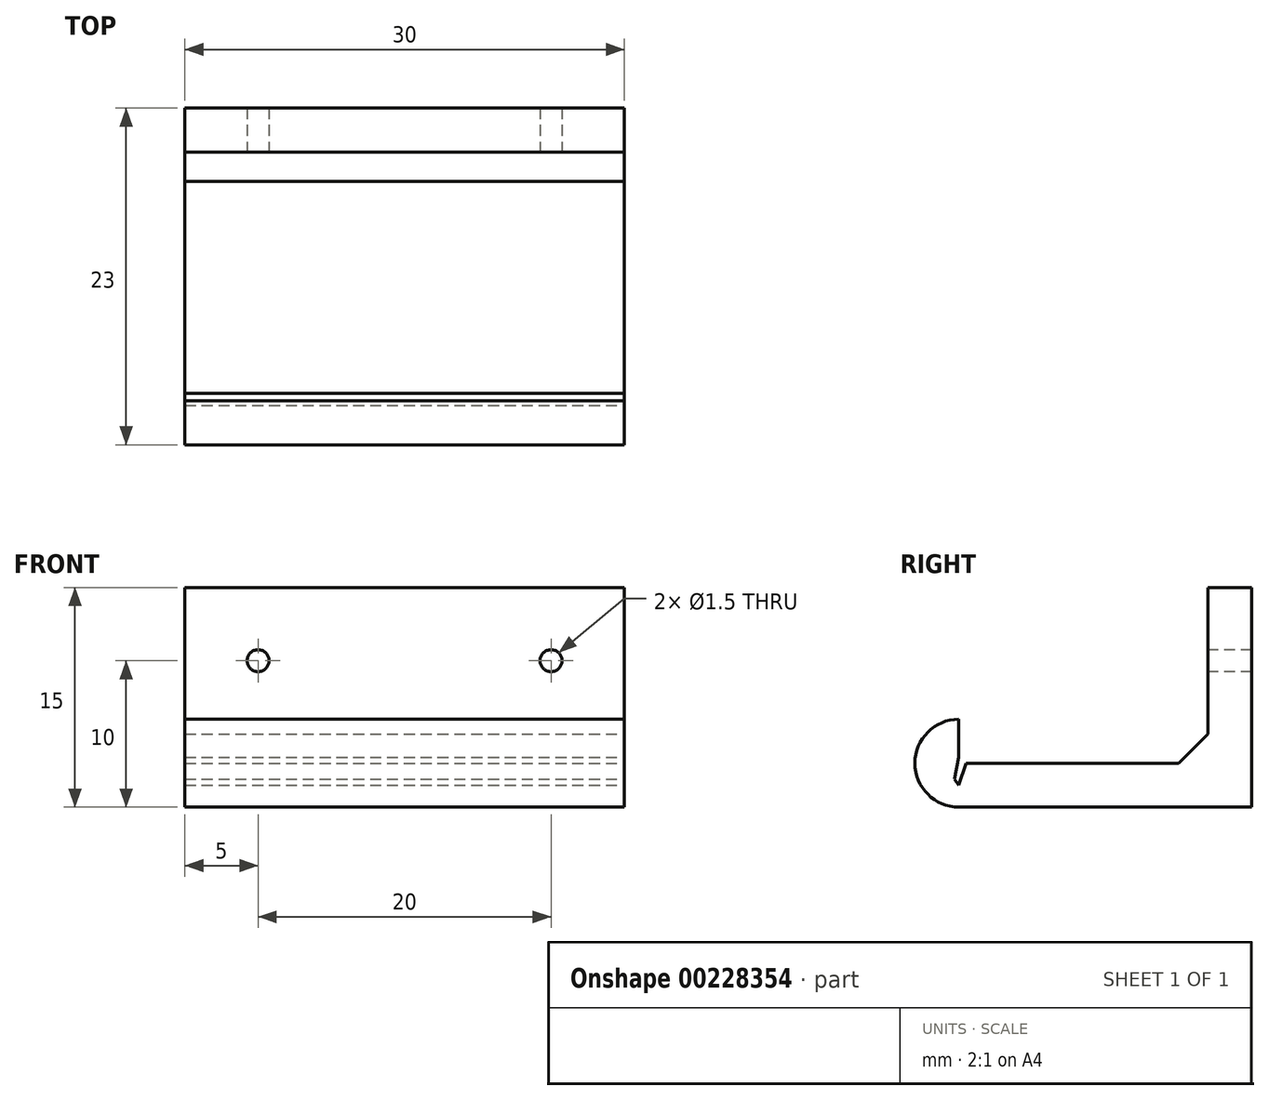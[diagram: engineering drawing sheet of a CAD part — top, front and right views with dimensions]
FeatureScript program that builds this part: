
annotation { "Feature Type Name" : "Feature", "Feature Type Description" : "" }
export const myFeature = defineFeature(function(context is Context, id is Id, definition is map)
    precondition{}
    {
        {
            var Q0;
            Q0=qCreatedBy(makeId("Right.planeOp"),FACE);
            var sketch = newSketch(context, id + "F0", { "sketchPlane" : qUnion([Q0])});
            skLineSegment(sketch, "E0", {"start": v(0, 0) * mm, "end": v(-20, 0) * mm});
            skLineSegment(sketch, "E1", {"start": v(-20, 0) * mm, "end": v(-20, 3) * mm});
            skLineSegment(sketch, "E2", {"start": v(0, 0) * mm, "end": v(0, 15) * mm});
            skLineSegment(sketch, "E3", {"start": v(0, 15) * mm, "end": v(-3, 15) * mm});
            skLineSegment(sketch, "E4", {"start": v(-3, 15) * mm, "end": v(-3, 5) * mm});
            skLineSegment(sketch, "E5", {"start": v(-20, 3) * mm, "end": v(-5, 3) * mm});
            skLineSegment(sketch, "E6", {"start": v(-5, 3) * mm, "end": v(-3, 5) * mm});
            skArc(sketch, "E7", {"start": v(-20, 0) * mm, "mid": v(-23, 3) * mm, "end": v(-20, 6) * mm});
            skLineSegment(sketch, "E8", {"start": v(-20, 6) * mm, "end": v(-20, 3) * mm});
            skSolve(sketch);
        }
        {
            var Q0;
            Q0 = qSketchRegion(id + "F0", true);
            extrude(context, id + "F1", {"entities" : qUnion([Q0]), "oppositeDirection" : true, "depth" : 30 * mm});
        }
        {
            var Q0;
            Q0=makeQuery(id+"F1.opExtrude","SWEPT_FACE",FACE,{"disambiguationData":[OSD([sQuery(id+"F0.wireOp",EDGE,"E4")])]});
            var sketch = newSketch(context, id + "F2", { "sketchPlane" : qUnion([Q0])});
            skPoint(sketch, "E9.0", {"position": v(-30, 15) * mm});
            skPoint(sketch, "E10.0", {"position": v(0, 15) * mm});
            skLineSegment(sketch, "E11.0", {"start": v(-30, 15) * mm, "end": v(0, 15) * mm});
            skLineSegment(sketch, "E11.1", {"start": v(-30, 15) * mm, "end": v(-30, 5) * mm});
            skLineSegment(sketch, "E11.2", {"start": v(0, 15) * mm, "end": v(0, 5) * mm});
            skLineSegment(sketch, "E12", {"start": v(-15, 15) * mm, "end": v(-15, 5) * mm});
            skLineSegment(sketch, "E13.0", {"start": v(-25, 15) * mm, "end": v(-25, 5) * mm});
            skLineSegment(sketch, "E14.MirrorCS", {"start": v(-5, 15) * mm, "end": v(-5, 5) * mm});
            skLineSegment(sketch, "E15.0", {"start": v(-30, 10) * mm, "end": v(0, 10) * mm});
            skPoint(sketch, "E16", {"position": v(-25, 10) * mm});
            skPoint(sketch, "E17", {"position": v(-5, 10) * mm});
            skSolve(sketch);
        }
        {
            var Q0;
            Q0=sQuery(id+"F2.wireOp",VERTEX,"E16");
            var Q1;
            Q1=sQuery(id+"F2.wireOp",VERTEX,"E17");
            var Q2;
            Q2=makeQuery(id+"F1.opExtrude","SWEPT_BODY",BODY,{"disambiguationData":[OSD([sQuery(id+"F0.wireOp",EDGE,"E0"),sQuery(id+"F0.wireOp",EDGE,"E2"),sQuery(id+"F0.wireOp",EDGE,"E3"),sQuery(id+"F0.wireOp",EDGE,"E4"),sQuery(id+"F0.wireOp",EDGE,"E5"),sQuery(id+"F0.wireOp",EDGE,"E6"),sQuery(id+"F0.wireOp",EDGE,"E7"),sQuery(id+"F0.wireOp",EDGE,"E8")])]});
            hole(context, id + "F3", {"style" : HoleStyle.SIMPLE, "endStyle" : HoleEndStyle.THROUGH, "holeDiameter" : 1.5 * mm, "locations" : qUnion([Q0, Q1]), "scope" : qUnion([Q2]), "isTappedThrough" : true});
        }
        {
            var Q0;
            Q0=makeQuery(id+"F0.imprint","IMPRINT",FACE,{"disambiguationData":[TD([[makeQuery(id+"F0.imprint","IMPRINT",EDGE,{"derivedFrom":sQuery(id+"F0.wireOp",EDGE,"E0")}),-1.0]])]});
            var sketch = newSketch(context, id + "F4", { "sketchPlane" : qUnion([Q0])});
            skPoint(sketch, "E18.0", {"position": v(-20, 3) * mm});
            skLineSegment(sketch, "E19", {"start": v(-20, 3) * mm, "end": v(-20, 3.4) * mm});
            skLineSegment(sketch, "E20", {"start": v(-20, 3) * mm, "end": v(-19.5, 3) * mm});
            skLineSegment(sketch, "E21", {"start": v(-20, 3) * mm, "end": v(-20, 1.5) * mm, "construction": true});
            skLineSegment(sketch, "E22", {"start": v(-19.5, 3) * mm, "end": v(-20, 1.5) * mm});
            skLineSegment(sketch, "E23", {"start": v(-20, 3.4) * mm, "end": v(-20.3, 1.9) * mm});
            skLineSegment(sketch, "E24", {"start": v(-20.3, 1.9) * mm, "end": v(-20, 1.5) * mm});
            skSolve(sketch);
        }
        {
            var Q0;
            {var subQ0=sQuery(id+"F4.wireOp",EDGE,"E20");Q0=makeQuery(id+"F4.imprint","IMPRINT",FACE,{"disambiguationData":[TD([[makeQuery(id+"F4.imprint","IMPRINT",EDGE,{"derivedFrom":subQ0}),-1.0]])]});}
            var Q1;
            {var subQ0=sQuery(id+"F4.wireOp",EDGE,"E19");Q1=makeQuery(id+"F4.imprint","IMPRINT",FACE,{"disambiguationData":[TD([[makeQuery(id+"F4.imprint","IMPRINT",EDGE,{"derivedFrom":subQ0}),1.0]])]});}
            extrude(context, id + "F5", {"entities" : qUnion([Q0, Q1]), "operationType" : NewBodyOperationType.REMOVE, "oppositeDirection" : true, "depth" : 30 * mm});
        }
    });
